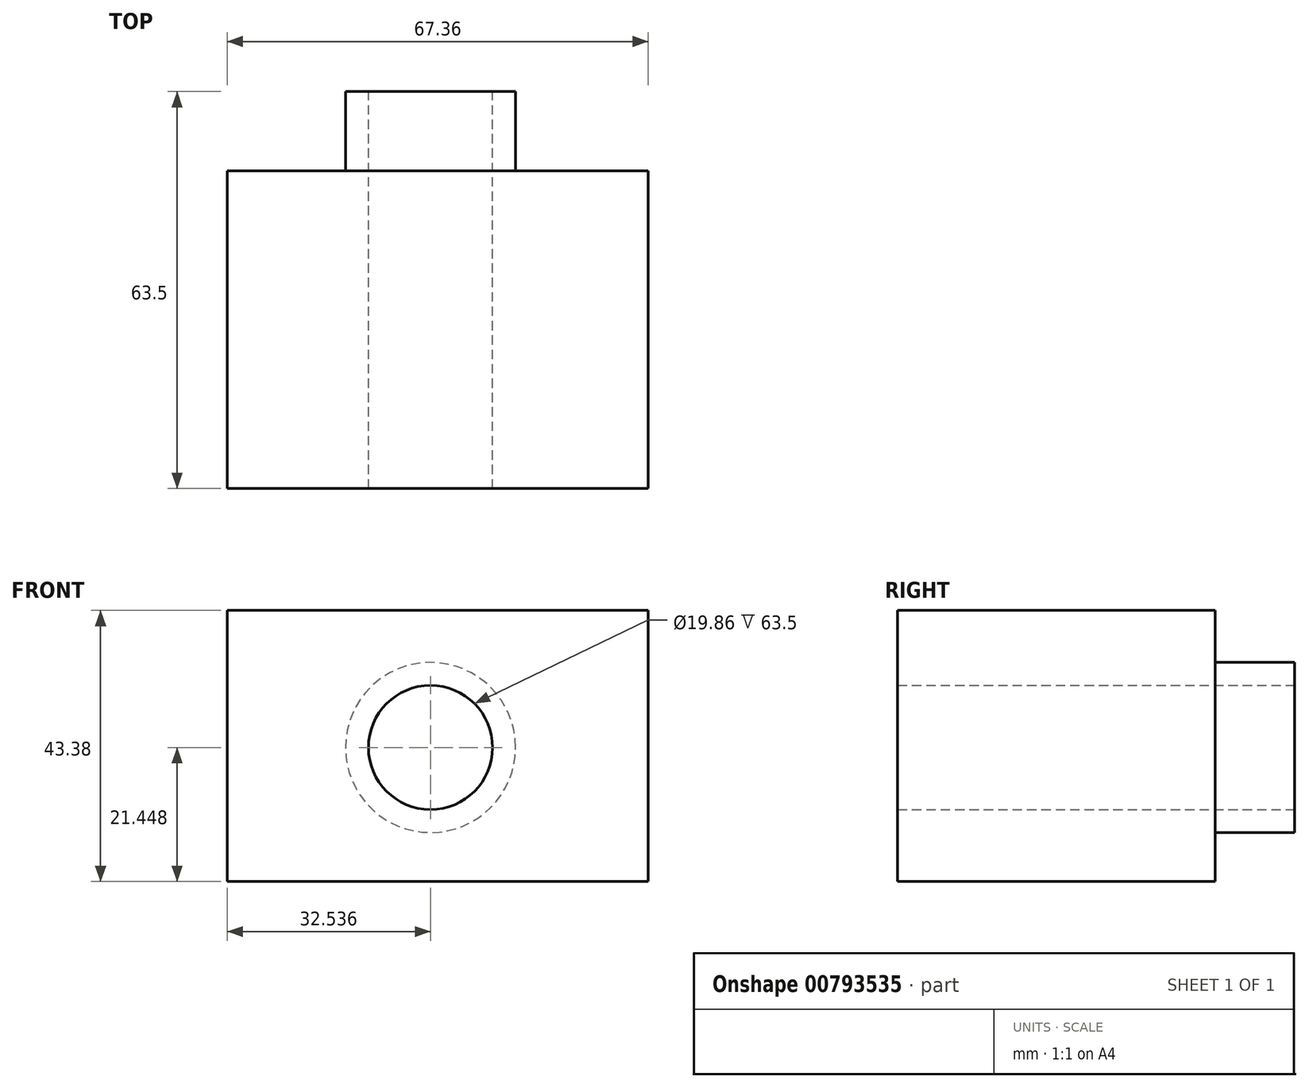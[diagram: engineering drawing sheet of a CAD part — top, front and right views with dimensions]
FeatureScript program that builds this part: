
annotation { "Feature Type Name" : "Feature", "Feature Type Description" : "" }
export const myFeature = defineFeature(function(context is Context, id is Id, definition is map)
    precondition{}
    {
        {
            var Q0;
            Q0=qCreatedBy(makeId("Front.planeOp"),FACE);
            var sketch = newSketch(context, id + "F0", { "sketchPlane" : qUnion([Q0])});
            skLineSegment(sketch, "E0.bottom", {"start": v(0, 2.29) * mm, "end": v(-67.36, 2.29) * mm});
            skLineSegment(sketch, "E0.top", {"start": v(0, 45.67) * mm, "end": v(-67.36, 45.67) * mm});
            skLineSegment(sketch, "E0.left", {"start": v(0, 2.29) * mm, "end": v(0, 45.67) * mm});
            skLineSegment(sketch, "E0.right", {"start": v(-67.36, 2.29) * mm, "end": v(-67.36, 45.67) * mm});
            skSolve(sketch);
        }
        {
            var Q0;
            Q0=makeQuery(id+"F0.imprint","IMPRINT",FACE,{"disambiguationData":[TD([[makeQuery(id+"F0.imprint","IMPRINT",EDGE,{"derivedFrom":sQuery(id+"F0.wireOp",EDGE,"E0.bottom")}),-1.0]])]});
            extrude(context, id + "F1", {"entities" : qUnion([Q0]), "depth" : 50.8 * mm, "offsetDistance" : 25.4 * mm});
        }
        {
            var Q0;
            Q0=makeQuery(id+"F1.opExtrude","CAP_FACE",FACE,{"disambiguationData":[OSD([sQuery(id+"F0.wireOp",EDGE,"E0.bottom"),sQuery(id+"F0.wireOp",EDGE,"E0.top"),sQuery(id+"F0.wireOp",EDGE,"E0.left"),sQuery(id+"F0.wireOp",EDGE,"E0.right")])],"isStart":true});
            var sketch = newSketch(context, id + "F2", { "sketchPlane" : qUnion([Q0])});
            skCircle(sketch, "E1", {"center": v(34.82, 23.74) * mm, "radius": 13.6 * mm});
            skCircle(sketch, "E2", {"center": v(34.82, 23.74) * mm, "radius": 9.93 * mm});
            skSolve(sketch);
        }
        {
            var Q0;
            Q0=makeQuery(id+"F2.imprint","IMPRINT",FACE,{"disambiguationData":[TD([[makeQuery(id+"F2.imprint","IMPRINT",EDGE,{"derivedFrom":sQuery(id+"F2.wireOp",EDGE,"E2")}),1.0]])]});
            extrude(context, id + "F3", {"entities" : qUnion([Q0]), "operationType" : NewBodyOperationType.REMOVE, "oppositeDirection" : true, "depth" : 50.8 * mm, "offsetDistance" : 25.4 * mm});
        }
        {
            var Q0;
            Q0=makeQuery(id+"F2.imprint","IMPRINT",FACE,{"disambiguationData":[TD([[makeQuery(id+"F2.imprint","IMPRINT",EDGE,{"derivedFrom":sQuery(id+"F2.wireOp",EDGE,"E1")}),1.0]])]});
            extrude(context, id + "F4", {"entities" : qUnion([Q0]), "operationType" : NewBodyOperationType.ADD, "depth" : 12.7 * mm, "offsetDistance" : 25.4 * mm});
        }
    });
